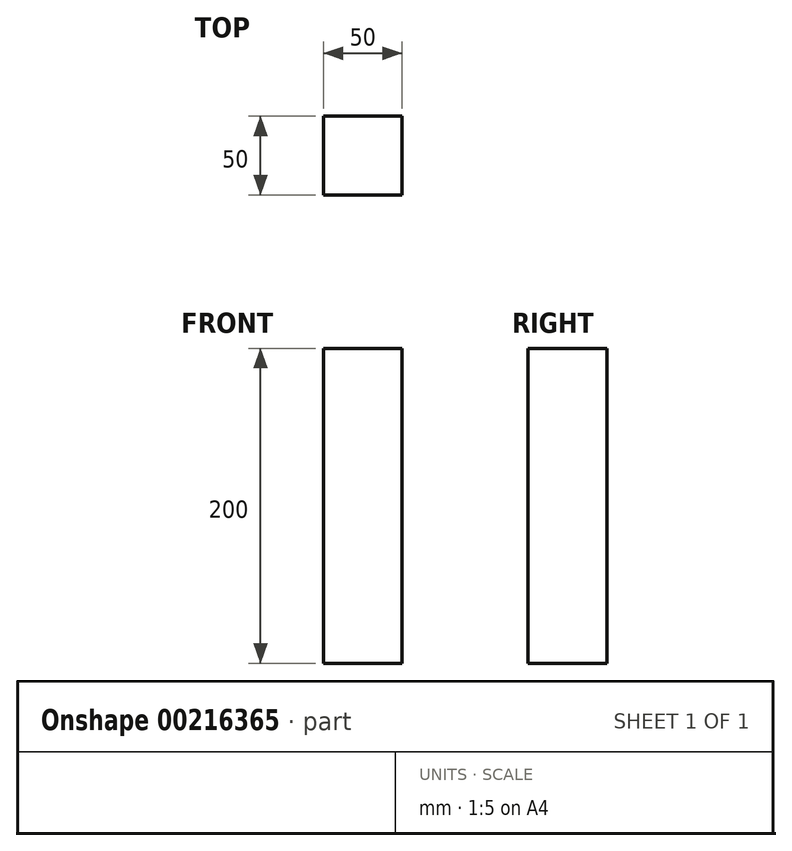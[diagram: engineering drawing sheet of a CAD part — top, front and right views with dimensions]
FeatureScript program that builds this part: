
annotation { "Feature Type Name" : "Feature", "Feature Type Description" : "" }
export const myFeature = defineFeature(function(context is Context, id is Id, definition is map)
    precondition{}
    {
        {
            var Q0;
            Q0=qCreatedBy(makeId("Top.planeOp"),FACE);
            var sketch = newSketch(context, id + "F0", { "sketchPlane" : qUnion([Q0])});
            skLineSegment(sketch, "E0.bottom", {"start": v(-96.04, -56.98) * mm, "end": v(-46.04, -56.98) * mm});
            skLineSegment(sketch, "E0.top", {"start": v(-96.04, -106.98) * mm, "end": v(-46.04, -106.98) * mm});
            skLineSegment(sketch, "E0.left", {"start": v(-96.04, -56.98) * mm, "end": v(-96.04, -106.98) * mm});
            skLineSegment(sketch, "E0.right", {"start": v(-46.04, -56.98) * mm, "end": v(-46.04, -106.98) * mm});
            skSolve(sketch);
        }
        {
            var Q0;
            Q0 = qSketchRegion(id + "F0", true);
            extrude(context, id + "F1", {"entities" : qUnion([Q0]), "depth" : 200 * mm, "offsetDistance" : 25 * mm});
        }
    });
